# Revit family: ISI_IdealStandard_PedestalWashBasins_Tempo-40cm
name_source: partatom
category: Plumbing Fixtures
revit_build: Autodesk Revit MEP 2012 (Build: 20110309_2315(x64)
units: mm (PartAtom-declared; Revit-internal decimal feet)

## types (2) — shared parameters
Accessories = www.idealspec.co.uk
AreaUnits = millimeters
Assembly Code = C1030200
AssetType = Fixed
BIMObjectName = ISI_IdealStandard_WallHungHandRinseBasins_Tempo_T0593
Brand = Ideal Standard
Category = SanitaryTerminal_WASHHANDBASIN_UK
Color = White
ConnectionType = Plumbing
Default Elevation = 815 mm  [stored 2.67388 ft]
DrainSize = 32 mm  [stored 0.104987 ft]
DurationUnit = year
ECA = No
ExpectedLife = 30
Features = 40 cm handrinse washbasin, one taphole
Finish = White
IfcExportAs = IfcSanitaryTerminalType
IfcExportType = WASHHANDBASIN
InstallationInstructions = www.idealspec.co.uk/resources.html
LinearUnits = millimeters
ManufacturerURL = www.idealspec.co.uk
Material = Vitreous china
NBSDescription = Wall hung hand rinse basins
NBSReference = 45-35-70/368
Name = WallHungWashBasins_Tempo_T0593_IdealStandard
NettWeight = 8 Kg
NominalDepth = 361 mm
NominalHeight = 815 mm  [stored 2.67388 ft]
NominalLength = 361 mm
NominalWidth = 400 mm  [stored 1.31234 ft]
ProductInformation = www.idealspec.co.uk/assets/datasheet/T059301
Shape = Sculptured
Size = 400 x 360 x 815 mm
Space = Internal
SpareParts = www.fastpart-spares.co.uk
URL = www.idealspec.co.uk
Uniclass2 = Pr_40_20_96_95
Version = 2
VolumeUnits = Litres
WRAS = No
WarrantyDescription = Manufacturers Warranty
WarrantyDurationParts = 99
WarrantyDurationUnit = year
WashHandBasinMounting = WallHung
WashHandBasinType = HandRinse
WaterEfficientProduct = No
zero-valued in all types: CWFU, HWFU, WFU

## per-type parameters (varying)
| type | 1TH | 2TH | Description | Model | ModelNumber | ModelReference |
| T059301 - Tempo 40cm handrinse washbasin, one taphole | Yes | No | Tempo 40 cm handrinse washbasin, one taphole | T059301 | T059301 | Tempo 40 cm handrinse washbasin, one taphole |
| T059401 - Tempo 40cm handrinse washbasin, two tapholes | No | Yes | Tempo 40 cm handrinse washbasin, two taphole | T059401 | T059401 | Tempo 40 cm handrinse washbasin, two taphole |

note: [stored X ft] marks values corroborated as IEEE doubles in the binary element streams (Revit-internal decimal feet)

## geometry (parser evidence)
native form markers: Sweep x12
no freeform markers — native parametric forms only
